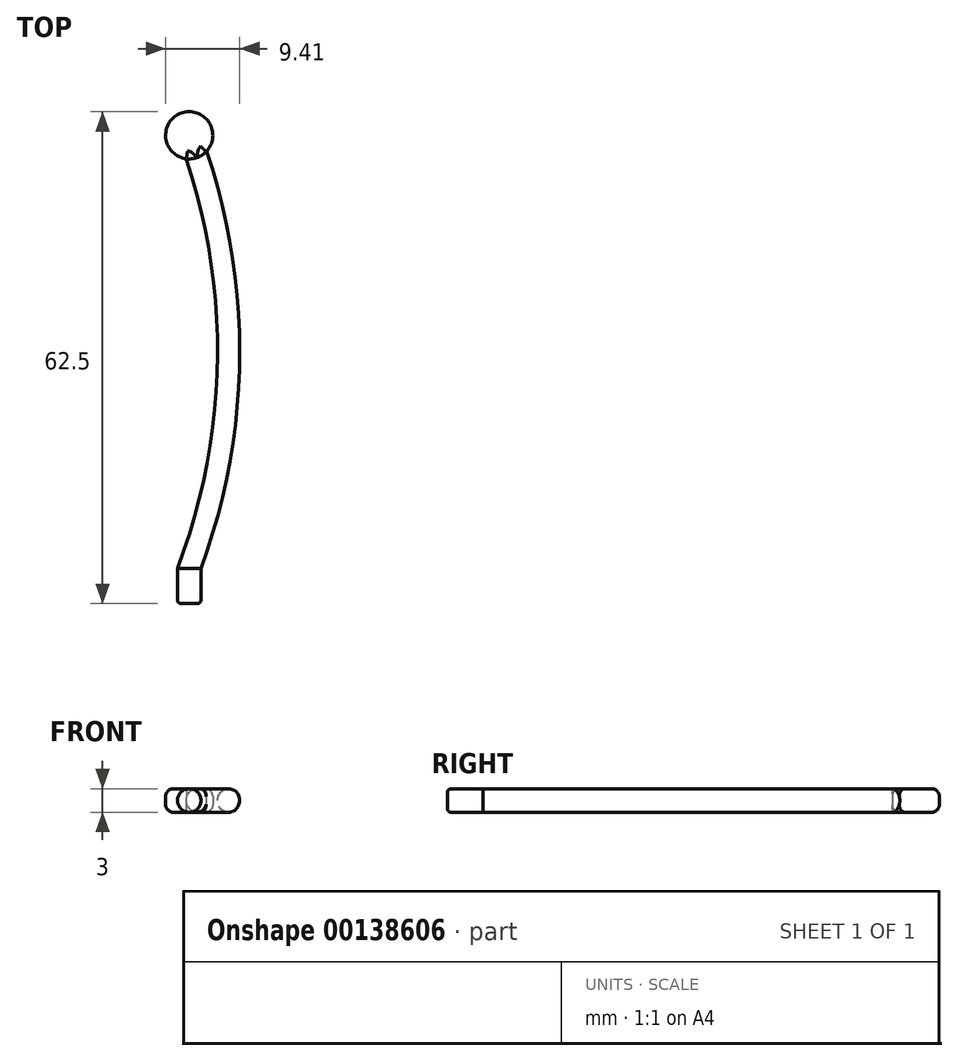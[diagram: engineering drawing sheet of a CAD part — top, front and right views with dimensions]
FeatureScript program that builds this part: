
annotation { "Feature Type Name" : "Feature", "Feature Type Description" : "" }
export const myFeature = defineFeature(function(context is Context, id is Id, definition is map)
    precondition{}
    {
        {
            assignVariable(context, id + "F0", {"name" : "pin_dia", "anyValue" : 3 * mm});
        }
        {
            assignVariable(context, id + "F1", {"name" : "pin_end_fillet", "anyValue" : 0.5 * mm});
        }
        {
            assignVariable(context, id + "F2", {"name" : "pin_length", "anyValue" : 4.5 * mm});
        }
        {
            var Q0;
            Q0=qCreatedBy(makeId("Top.planeOp"),FACE);
            var sketch = newSketch(context, id + "F3", { "sketchPlane" : qUnion([Q0])});
            skLineSegment(sketch, "E0", {"start": v(0, 0) * mm, "end": v(0, 55) * mm, "construction": true});
            skLineSegment(sketch, "E1", {"start": v(0, 27.5) * mm, "end": v(5, 27.5) * mm, "construction": true});
            skPoint(sketch, "E1.endSnap0", {"position": v(0, 27.5) * mm});
            skArc(sketch, "E2", {"start": v(0, 0) * mm, "mid": v(5, 27.5) * mm, "end": v(0, 55) * mm});
            skCircle(sketch, "E3", {"center": v(0, 55) * mm, "radius": 3 * mm});
            skSolve(sketch);
        }
        {
            var Q0;
            Q0=qCreatedBy(makeId("Front.planeOp"),FACE);
            var sketch = newSketch(context, id + "F4", { "sketchPlane" : qUnion([Q0])});
            skPoint(sketch, "E4.0", {"position": v(0, 0) * mm});
            skCircle(sketch, "E5", {"center": v(0, 0) * mm, "radius": 1.5 * mm});
            skSolve(sketch);
        }
        {
            var Q0;
            Q0=makeQuery(id+"F4.imprint","IMPRINT",FACE,{"disambiguationData":[TD([[makeQuery(id+"F4.imprint","IMPRINT",EDGE,{"derivedFrom":sQuery(id+"F4.wireOp",EDGE,"E5")}),1.0]])]});
            var Q1;
            Q1=sQuery(id+"F3.wireOp",EDGE,"E2");
            sweep(context, id + "F5", {"profiles" : qUnion([Q0]), "path" : qUnion([Q1])});
        }
        {
            var Q0;
            Q0 = qSketchRegion(id + "F3", true);
            extrude(context, id + "F6", {"entities" : qUnion([Q0]), "operationType" : NewBodyOperationType.ADD, "depth" : getVariable(context, 'pin_dia') / 2, "hasSecondDirection" : true, "secondDirectionOppositeDirection" : true, "secondDirectionDepth" : getVariable(context, 'pin_dia') / 2});
        }
        {
            var Q0;
            Q0=makeQuery(id+"F6.opExtrude","CAP_EDGE",EDGE,{"disambiguationData":[OSD([sQuery(id+"F3.wireOp",EDGE,"E3")])],"isStart":false});
            var Q1;
            Q1=makeQuery(id+"F6.opExtrude","CAP_EDGE",EDGE,{"disambiguationData":[OSD([sQuery(id+"F3.wireOp",EDGE,"E3")])],"isStart":true});
            fillet(context, id + "F7", {"entities" : qUnion([Q0, Q1]), "radius" : (getVariable(context, 'pin_dia')) - 2 * mm, "tangentPropagation" : true, "allowEdgeOverflow" : false});
        }
        {
            var Q0;
            Q0=makeQuery(id+"F5.opSweep","CAP_FACE",FACE,{"disambiguationData":[OSD([sQuery(id+"F3.wireOp",VERTEX,"E2.start"),sQuery(id+"F4.wireOp",EDGE,"E5")])],"isStart":true});
            var Q1;
            Q1 = qConstructionFilter(qBodyType(qCreatedBy(id + "F4" ,EDGE), BodyType.WIRE), ConstructionObject.NO);
            extrude(context, id + "F8", {"entities" : qUnion([Q0]), "operationType" : NewBodyOperationType.ADD, "surfaceEntities" : qUnion([Q1]), "depth" : getVariable(context, 'pin_length')});
        }
        {
            var Q0;
            Q0=makeQuery(id+"F8.opExtrude","CAP_EDGE",EDGE,{"disambiguationData":[OSD([sQuery(id+"F3.wireOp",VERTEX,"E2.start"),sQuery(id+"F4.wireOp",EDGE,"E5")])],"isStart":false});
            fillet(context, id + "F9", {"entities" : qUnion([Q0]), "radius" : getVariable(context, 'pin_end_fillet'), "tangentPropagation" : true, "allowEdgeOverflow" : false});
        }
    });
